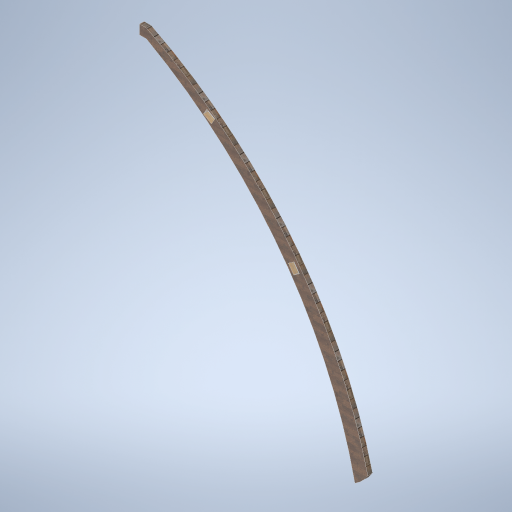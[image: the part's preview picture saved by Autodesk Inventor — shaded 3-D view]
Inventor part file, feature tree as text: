
AUTODESK INVENTOR PART (.ipt)
format: ipt  version: 2024.2 (Build 282272000, 272)  size: 309,248 bytes
history: native  units: mm
features: extrude x2, sketch x2
ambient origin geometry x8: Origin, YZ Plane, XZ Plane, XY Plane, X Axis, Y Axis, Z Axis, Center Point
bodies: Solid1 (feature_tree)
feature tree (4):
  extrude  "Extrusion1"  Depth=150.0mm
  extrude  "Extrusion3"  Depth=200.0mm
  sketch  "Sketch1"  dims[d0=9000.0mm d1=9000.0mm d2=150.0mm]
  sketch  "Sketch2"  dims[d3=100.0mm d4=0.0mm d8=200.0mm d9=9.599311mm d10=150.0mm d13=200.0mm d14=30.0deg d15=150.0mm d16=0.0mm d17=0.0mm]
